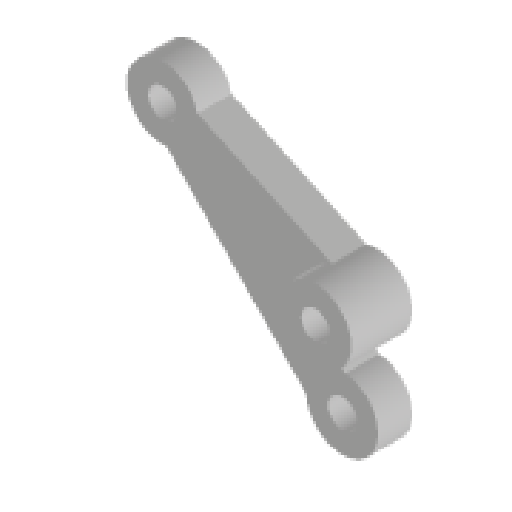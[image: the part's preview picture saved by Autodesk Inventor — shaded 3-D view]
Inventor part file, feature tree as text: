
AUTODESK INVENTOR PART (.ipt)
format: ipt  version: 2025.1 (Build 291241020, 241B)  size: 145,408 bytes
history: native  units: in
note: dims shown in document units (in); Inventor stores cm internally (conversion verified against a paired STEP export)
features: extrude x2, sketch x2
ambient origin geometry x8: Origin, YZ Plane, XZ Plane, XY Plane, X Axis, Y Axis, Z Axis, Center Point
bodies: Solid1 (feature_tree)
feature tree (4):
  extrude  "Extrusion1"  Depth=0.16in
  extrude  "Extrusion4"  Depth=0.15in
  sketch  "Sketch1"  dims[d0=0.4in d1=0.16in]
  sketch  "Sketch4"  dims[d7=0.4in d8=0.16in d9=0.5in d10=0.3in d11=0.15in d12=60.0deg d14=0.19in d15=0.0in d20=0.4in d21=0.16in d25=0.3in d29=1.0in d30=0.3in d31=0.15in d32=1.0in d33=0.1718in d34=0.15in d35=0.0in]
